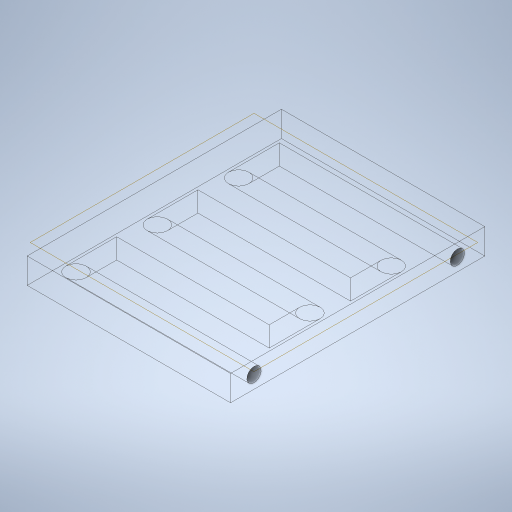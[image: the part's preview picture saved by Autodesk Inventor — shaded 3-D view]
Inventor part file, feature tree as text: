
AUTODESK INVENTOR PART (.ipt)
format: ipt  version: 2024.2 (Build 282272000, 272)  size: 286,720 bytes
history: native  units: in
note: dims shown in document units (in); Inventor stores cm internally (conversion verified against a paired STEP export)
features: sketch x3, plane x1, extrude x1, sweep x1
ambient origin geometry x8: Origin, YZ Plane, XZ Plane, XY Plane, X Axis, Y Axis, Z Axis, Center Point
bodies: Body1 (feature_tree)
feature tree (6):
  plane  "Work Plane1"
  sketch  "Sketch8"  dims[d4=0.0625in d24=0.875in]
  sketch  "Sketch9"  dims[d25=0.2in d26=0.75in]
  extrude  "Extrusion4"  Depth=0.875in
  sweep  "Sweep2"
  sketch  "Sketch10"  dims[d27=0.2in d28=0.2in d29=0.07in d30=1.0in d32=1.25in d33=0.125in d34=0.0in d35=0.0in d36=0.0in]
